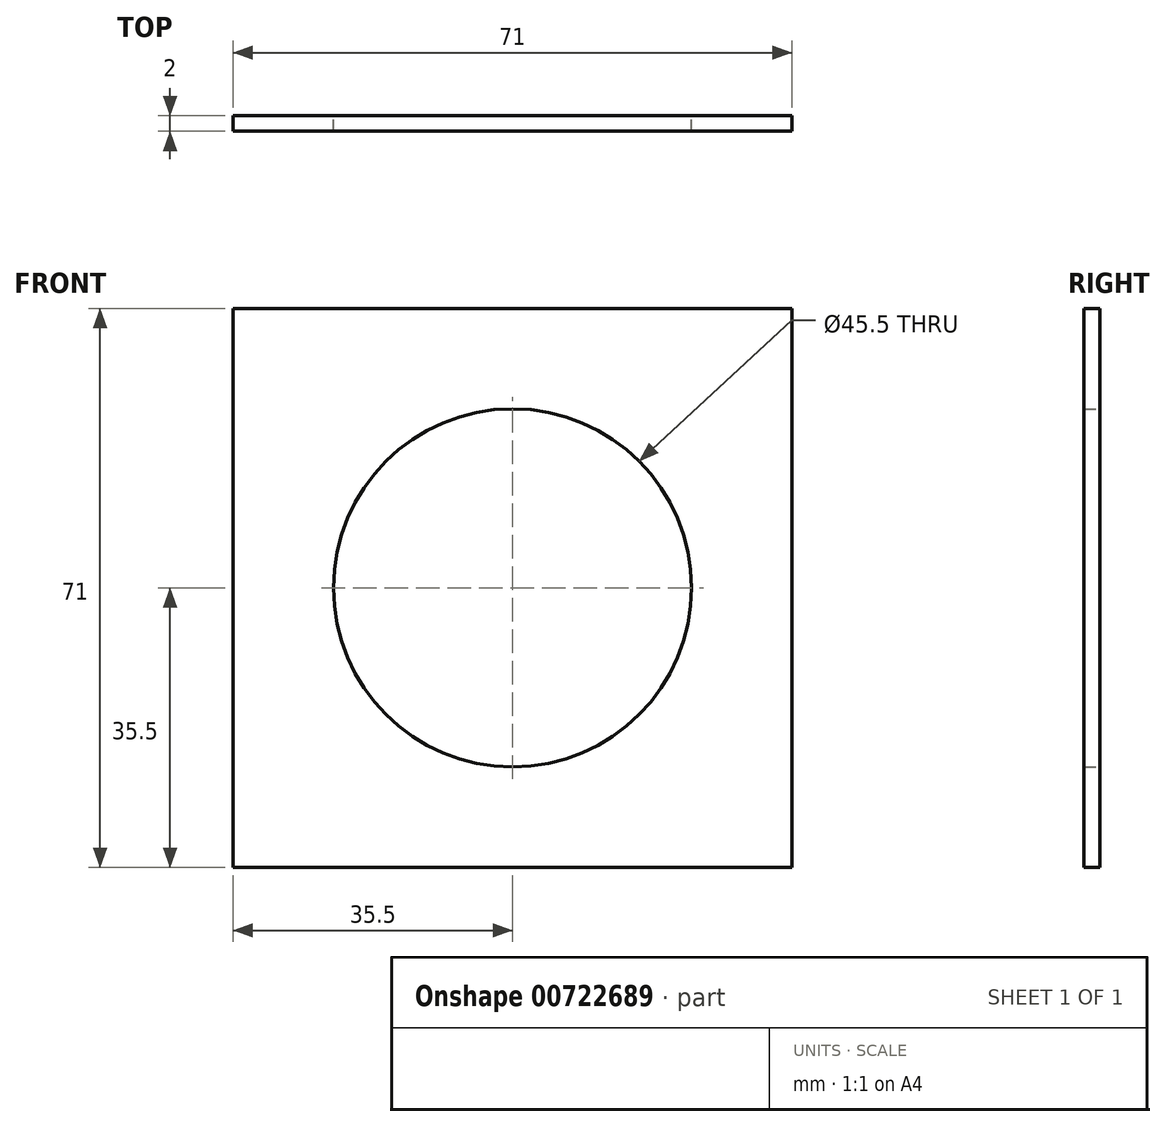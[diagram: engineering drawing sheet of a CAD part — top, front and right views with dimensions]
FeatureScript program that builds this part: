
annotation { "Feature Type Name" : "Feature", "Feature Type Description" : "" }
export const myFeature = defineFeature(function(context is Context, id is Id, definition is map)
    precondition{}
    {
        {
            var Q0;
            Q0=qCreatedBy(makeId("Front.planeOp"),FACE);
            var sketch = newSketch(context, id + "F0", { "sketchPlane" : qUnion([Q0])});
            skLineSegment(sketch, "E0.bottom", {"start": v(35.5, 35.5) * mm, "end": v(-35.5, 35.5) * mm});
            skLineSegment(sketch, "E0.top", {"start": v(35.5, -35.5) * mm, "end": v(-35.5, -35.5) * mm});
            skLineSegment(sketch, "E0.left", {"start": v(35.5, 35.5) * mm, "end": v(35.5, -35.5) * mm});
            skLineSegment(sketch, "E0.right", {"start": v(-35.5, 35.5) * mm, "end": v(-35.5, -35.5) * mm});
            skPoint(sketch, "E0.middle", {"position": v(0, 0) * mm});
            skCircle(sketch, "E1", {"center": v(0, 0) * mm, "radius": 22.75 * mm});
            skSolve(sketch);
        }
        {
            var Q0;
            Q0 = qSketchRegion(id + "F0", true);
            extrude(context, id + "F1", {"entities" : qUnion([Q0]), "depth" : 2 * mm, "offsetDistance" : 25 * mm, "symmetric" : true});
        }
    });
